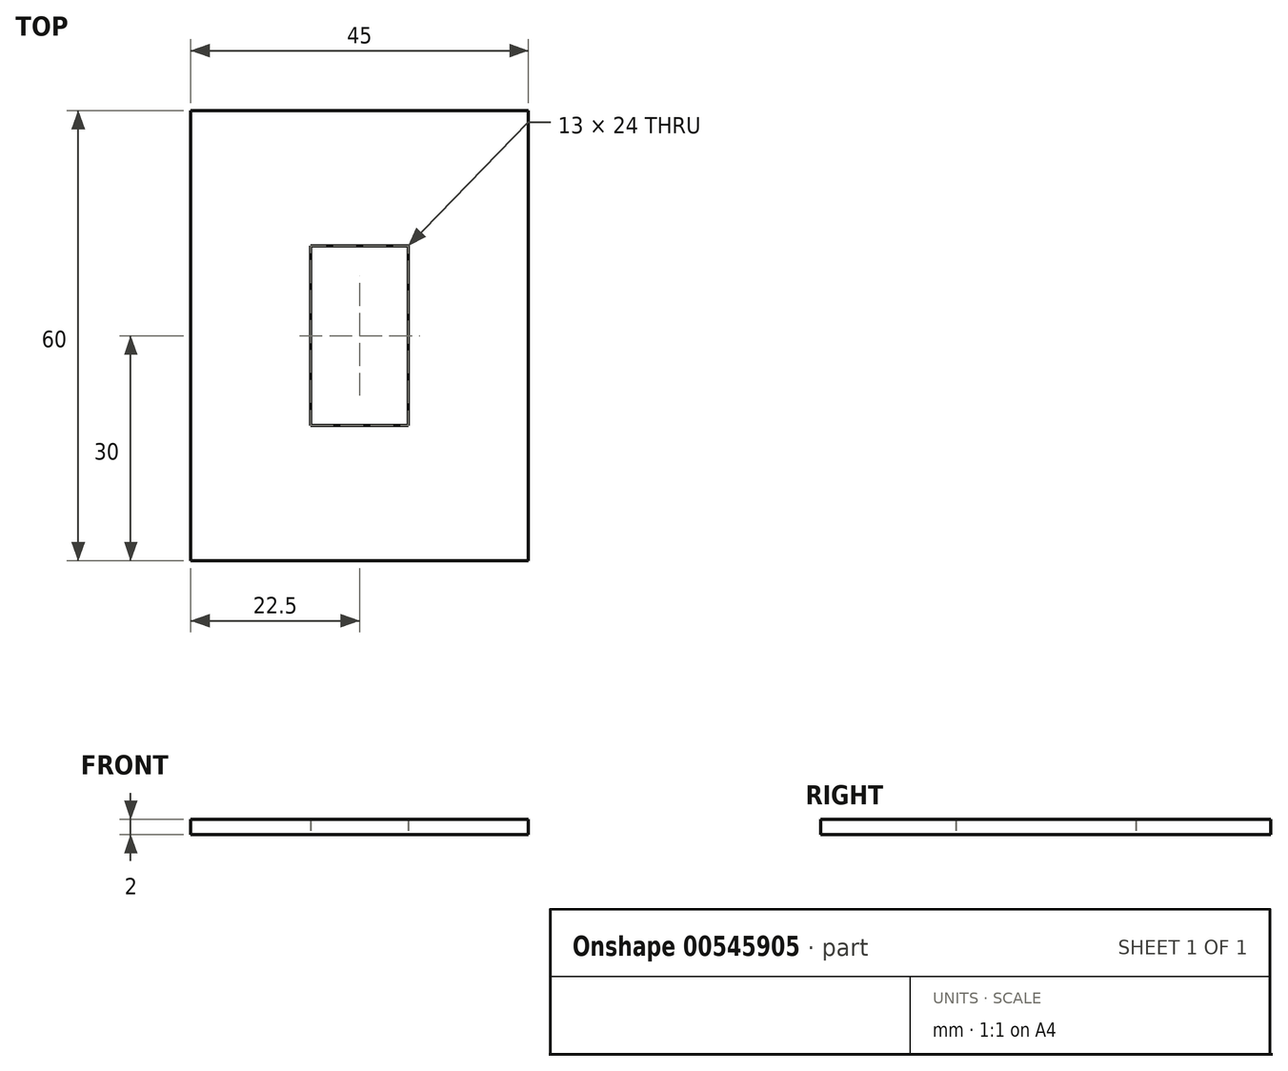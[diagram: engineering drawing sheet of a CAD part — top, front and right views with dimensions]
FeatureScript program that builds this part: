
annotation { "Feature Type Name" : "Feature", "Feature Type Description" : "" }
export const myFeature = defineFeature(function(context is Context, id is Id, definition is map)
    precondition{}
    {
        {
            var Q0;
            Q0=qCreatedBy(makeId("Top.planeOp"),FACE);
            var sketch = newSketch(context, id + "F0", { "sketchPlane" : qUnion([Q0])});
            skLineSegment(sketch, "E0.bottom", {"start": v(-47.5, -30) * mm, "end": v(-2.5, -30) * mm});
            skLineSegment(sketch, "E0.top", {"start": v(-47.5, 30) * mm, "end": v(-2.5, 30) * mm});
            skLineSegment(sketch, "E0.left", {"start": v(-47.5, -30) * mm, "end": v(-47.5, 30) * mm});
            skLineSegment(sketch, "E0.right", {"start": v(47.5, -30) * mm, "end": v(47.5, 30) * mm});
            skPoint(sketch, "E0.middle", {"position": v(0, 0) * mm});
            skLineSegment(sketch, "E1.bottom", {"start": v(-31.5, 12) * mm, "end": v(-18.5, 12) * mm});
            skLineSegment(sketch, "E1.top", {"start": v(-31.5, -12) * mm, "end": v(-18.5, -12) * mm});
            skLineSegment(sketch, "E1.left", {"start": v(-31.5, 12) * mm, "end": v(-31.5, -12) * mm});
            skLineSegment(sketch, "E1.right", {"start": v(-18.5, 12) * mm, "end": v(-18.5, -12) * mm});
            skLineSegment(sketch, "E2.bottom", {"start": v(18.5, 12) * mm, "end": v(31.5, 12) * mm});
            skLineSegment(sketch, "E2.top", {"start": v(18.5, -12) * mm, "end": v(31.5, -12) * mm});
            skLineSegment(sketch, "E2.left", {"start": v(18.5, 12) * mm, "end": v(18.5, -12) * mm});
            skLineSegment(sketch, "E2.right", {"start": v(31.5, 12) * mm, "end": v(31.5, -12) * mm});
            skLineSegment(sketch, "E3", {"start": v(-2.5, 30) * mm, "end": v(-2.5, -30) * mm});
            skLineSegment(sketch, "E4", {"start": v(2.5, 30) * mm, "end": v(2.5, -30) * mm});
            skPoint(sketch, "E5", {"position": v(-2.5, -30) * mm});
            skPoint(sketch, "E6", {"position": v(2.5, -30) * mm});
            skPoint(sketch, "E7", {"position": v(2.5, 30) * mm});
            skPoint(sketch, "E8", {"position": v(-2.5, 30) * mm});
            skLineSegment(sketch, "E9.trimOffspring", {"start": v(2.5, -30) * mm, "end": v(47.5, -30) * mm});
            skLineSegment(sketch, "E10.trimOffspring", {"start": v(2.5, 30) * mm, "end": v(47.5, 30) * mm});
            skSolve(sketch);
        }
        {
            var Q0;
            Q0=makeQuery(id+"F0.imprint","IMPRINT",FACE,{"disambiguationData":[TD([[makeQuery(id+"F0.imprint","IMPRINT",EDGE,{"derivedFrom":sQuery(id+"F0.wireOp",EDGE,"E0.bottom")}),1.0]])]});
            extrude(context, id + "F1", {"entities" : qUnion([Q0]), "depth" : 2 * mm});
        }
    });
